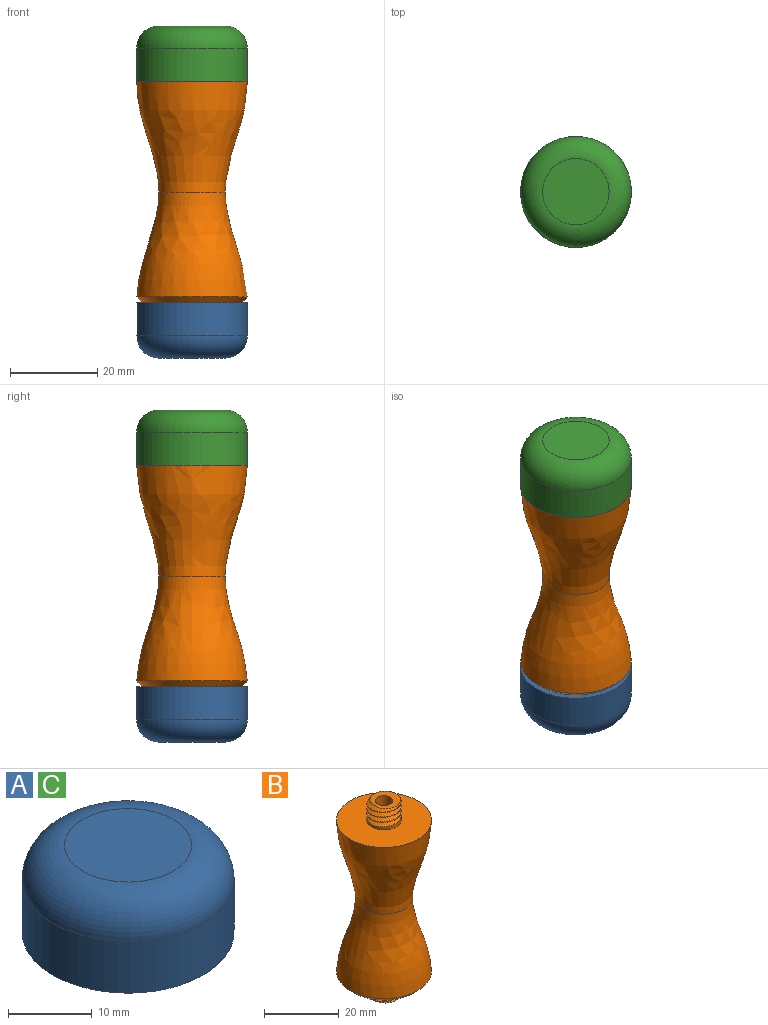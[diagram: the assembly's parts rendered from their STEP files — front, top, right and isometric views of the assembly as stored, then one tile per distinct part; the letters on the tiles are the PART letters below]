
ASSEMBLY  parts=3 mates=1
PART A: 8 faces, bbox 28.1x28.1x14.1 mm
  f0: plane 25.96x25.96mm, normal (0,0,-1), area 452.4mm2, adj f1,f2,f3,f7
  f1: bspline ~11.38x11.02mm, area 179.9mm2, adj f0,f2,f5,f7
  f2: bspline ~11.11x11.02mm, area 179.8mm2, adj f0,f1,f5,f7
  f3: cylinder r=12.7mm len=25.4mm, axis (0,0,-1), area 608mm2, adj f0,f6
  f4: plane 15.24x15.24mm, normal (0,0,1), area 182.4mm2, adj f6
  f5: plane 9.15x8.79mm, normal (0,0,-1), area 54.3mm2, adj f1,f2,f7
  f6: torus R=7.62mm, axis (0,0,1), area 544.2mm2, adj f3,f4
  f7: cylinder r=3.81mm len=9.53mm, axis (0,0,-1), area 68.9mm2, adj f0,f1,f2,f5
PART B: 34 faces, bbox 26.8x26.8x67.1 mm
  f0: revolved ~25.4x25.4mm, area 1671.5mm2, adj f1,f3
  f1: plane 25.4x25.4mm, normal (0,0,1), area 441mm2, adj f0,f4
  f2: plane 22.8x22.8mm, normal (0,0,-1), area 342.7mm2, adj f18,f33
  f3: revolved ~25.34x25.34mm, area 1565.6mm2, adj f0,f33
  f4: cylinder r=4.57mm len=9.14mm, axis (0,0,-1), area 26.4mm2, adj f1,f5,f14,f15,f16
  f5: cylinder r=4.57mm len=9.14mm, axis (0,0,-1), area 6.7mm2, adj f4,f6,f14,f15
  f6: cylinder r=4.57mm len=9.14mm, axis (0,0,-1), area 6.7mm2, adj f5,f7,f14,f15
  f7: cylinder r=4.57mm len=9.14mm, axis (0,0,-1), area 6.2mm2, adj f6,f14,f15,f17
  f8: revolved ~24.38x23.26mm, area 534.3mm2, adj f9,f10,f11
  f9: plane 18.62x4.64mm, normal (0,0,1), area 60.3mm2, adj f8,f11
  f10: revolved ~24.38x23.33mm, area 835mm2, adj f8,f11,f12
  f11: plane 50.22x21.76mm, normal (0.97,0,0.26), area 842.6mm2, adj f8,f9,f10,f12
  f12: plane 23.33x17.68mm, normal (0,0,-1), area 331.2mm2, adj f10,f11,f13
  f13: cylinder r=2.29mm len=7.37mm, axis (0,0,1), area 105.8mm2, adj f12,f17
  f14: bspline ~11x9.53mm, area 126.6mm2, adj f4,f5,f6,f7,f15,f16,f17
  f15: bspline ~11x9.53mm, area 111.2mm2, adj f4,f5,f6,f7,f14,f16,f17
  f16: plane 1.37x1.17mm, normal (-0.2,0.98,0), area 0.8mm2, adj f4,f14,f15
  f17: plane 9.06x8.84mm, normal (0,0,1), area 36mm2, adj f7,f13,f14,f15
  f18: cylinder r=4.57mm len=9.14mm, axis (0,0,1), area 26.1mm2, adj f2,f21,f29,f30
  f19: cylinder r=4.57mm len=9.14mm, axis (0,0,1), area 6.4mm2, adj f20,f22,f30,f31,f32
  f20: cylinder r=4.57mm len=9.14mm, axis (0,0,1), area 6.7mm2, adj f19,f21,f30,f31
  f21: cylinder r=4.57mm len=9.14mm, axis (0,0,1), area 6.6mm2, adj f18,f20,f30,f31
  f22: cylinder r=4.57mm len=1.22mm, axis (0,0,1), area 0mm2, adj f19,f31,f32
  f23: revolved ~24.38x23.26mm, area 534.3mm2, adj f24,f25,f26
  f24: plane 18.62x4.64mm, normal (0,0,-1), area 60.3mm2, adj f23,f26
  f25: revolved ~24.38x23.33mm, area 835mm2, adj f23,f26,f27
  f26: plane 50.22x21.76mm, normal (-0.97,0,-0.26), area 842.6mm2, adj f23,f24,f25,f27
  f27: plane 23.33x17.68mm, normal (0,0,1), area 331.2mm2, adj f25,f26,f28
  f28: cylinder r=2.29mm len=7.37mm, axis (0,0,-1), area 105.8mm2, adj f27,f32
  f29: plane 1.37x1.17mm, normal (-0.2,-0.98,0), area 0.8mm2, adj f18,f30,f31
  f30: bspline ~11x9.53mm, area 126.6mm2, adj f18,f19,f20,f21,f29,f31,f32
  f31: bspline ~11x9.53mm, area 111.2mm2, adj f19,f20,f21,f22,f29,f30,f32
  f32: plane 9.06x8.84mm, normal (0,0,-1), area 36mm2, adj f19,f22,f28,f30,f31
  f33: cone r=11.4mm half-angle=43.7deg, axis (0,0,1), area 138.8mm2, adj f2,f3
PART C: same geometry as A
PLACE A rot(axis=(1,0,0),180deg) t=(-4.11,15.51,-30.37)mm
PLACE B t=(-4.05,15.51,-4.97)mm
PLACE C t=(-4.11,15.51,20.43)mm
MATE fastened A.f0 <-> B.f33  axis (0,0,1) through (-4.05,15.51,-30.37)mm
